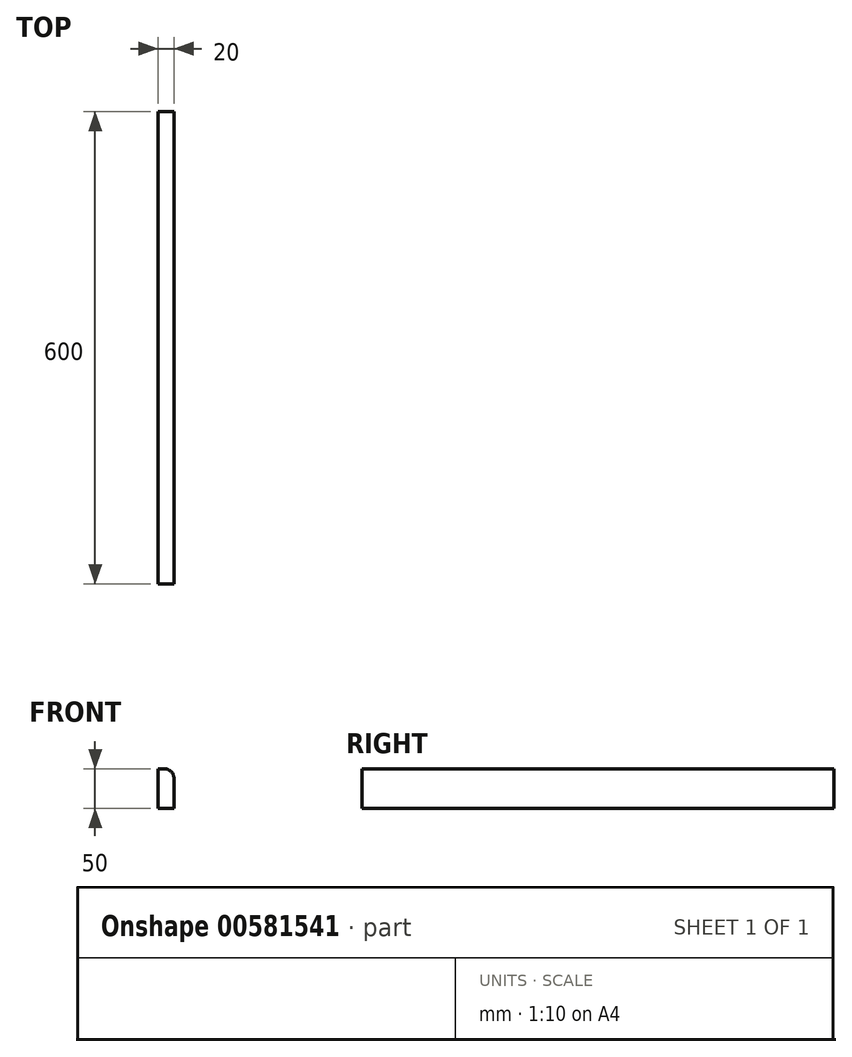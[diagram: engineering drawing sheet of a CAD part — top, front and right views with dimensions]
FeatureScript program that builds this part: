
annotation { "Feature Type Name" : "Feature", "Feature Type Description" : "" }
export const myFeature = defineFeature(function(context is Context, id is Id, definition is map)
    precondition{}
    {
        {
            var Q0;
            Q0=qCreatedBy(makeId("Top.planeOp"),FACE);
            var sketch = newSketch(context, id + "F0", { "sketchPlane" : qUnion([Q0])});
            skLineSegment(sketch, "E0.bottom", {"start": v(3.16, 585.23) * mm, "end": v(23.16, 585.23) * mm});
            skLineSegment(sketch, "E0.top", {"start": v(3.16, -14.77) * mm, "end": v(23.16, -14.77) * mm});
            skLineSegment(sketch, "E0.left", {"start": v(3.16, 585.23) * mm, "end": v(3.16, -14.77) * mm});
            skLineSegment(sketch, "E0.right", {"start": v(23.16, 585.23) * mm, "end": v(23.16, -14.77) * mm});
            skSolve(sketch);
        }
        {
            var Q0;
            Q0 = qSketchRegion(id + "F0", true);
            extrude(context, id + "F1", {"entities" : qUnion([Q0]), "depth" : 50 * mm, "offsetDistance" : 25 * mm});
        }
        {
            var Q0;
            Q0=makeQuery(id+"F1.opExtrude","CAP_EDGE",EDGE,{"disambiguationData":[OSD([sQuery(id+"F0.wireOp",EDGE,"E0.right")])],"isStart":false});
            fillet(context, id + "F2", {"entities" : qUnion([Q0]), "radius" : 12 * mm, "tangentPropagation" : true, "allowEdgeOverflow" : false});
        }
    });
